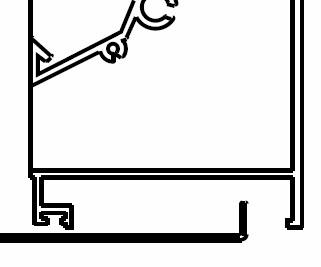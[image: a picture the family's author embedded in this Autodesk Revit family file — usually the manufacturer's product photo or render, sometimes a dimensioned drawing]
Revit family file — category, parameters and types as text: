
# Revit family: Louver_Carnes-Ext_Alum-Drainable-Stationary-FTBB
name_source: partatom
category: Duct Accessories
revit_build: Autodesk Revit MEP 2012 (Build: 20110309_2315(x64)
units: mm (PartAtom-declared; Revit-internal decimal feet)

## types (1)
- FTBB
    04 CSI = 08 91 00
    95 CSI = 10200
    Actual Height = 24"
    Actual Width = 24"
    Assembly Code = B2010300
    Blade Material = Metal - Carnes - Steel - Galvanized
    Blade Width = 22 39/128"
    Catalog URL = http://www.carnes.com
    Default Elevation = 0"
    Depth = 4 41/256"
    Description = Extruded Aluminum Stationary Drainable Blade Louver
    Duct Connector 1 = Duct Connection 1
    Duct Connector 2 = Duct Connection 2
    Frame Material = Metal - Carnes - Steel - Galvanized
    Height = 24"
    Manufacturer = CARNES COMPANY
    Manufacturer Fax = 608-845-6470
    Maximum Horinzontal Size = 120"W x 84"H
    Maximum System Pressure = 0.70 in-wg
    Maximum System Velocity = 1250 FPM
    Maximum Vertical Size = 84"W x 120"H
    Minimum Size = 12"W x 12"H
    Model = FTBB
    Offset = 3"
    Product Line = Extruded Aluminum Stationary Drainable Blade Louver
    Product Page URL = http://www.carnes.com
    Spec Sheet URL = http://www.carnes.com
    Subcategory = Louvers and Dampers
    URL = http://www.carnes.com
    Warranty URL = http://www.carnes.com
    Width = 24"
    ecoScorecard Product Page = http://ecoscorecard.com

## geometry (parser evidence)
native form markers: Blend x2, Sweep x7
no freeform markers — native parametric forms only
